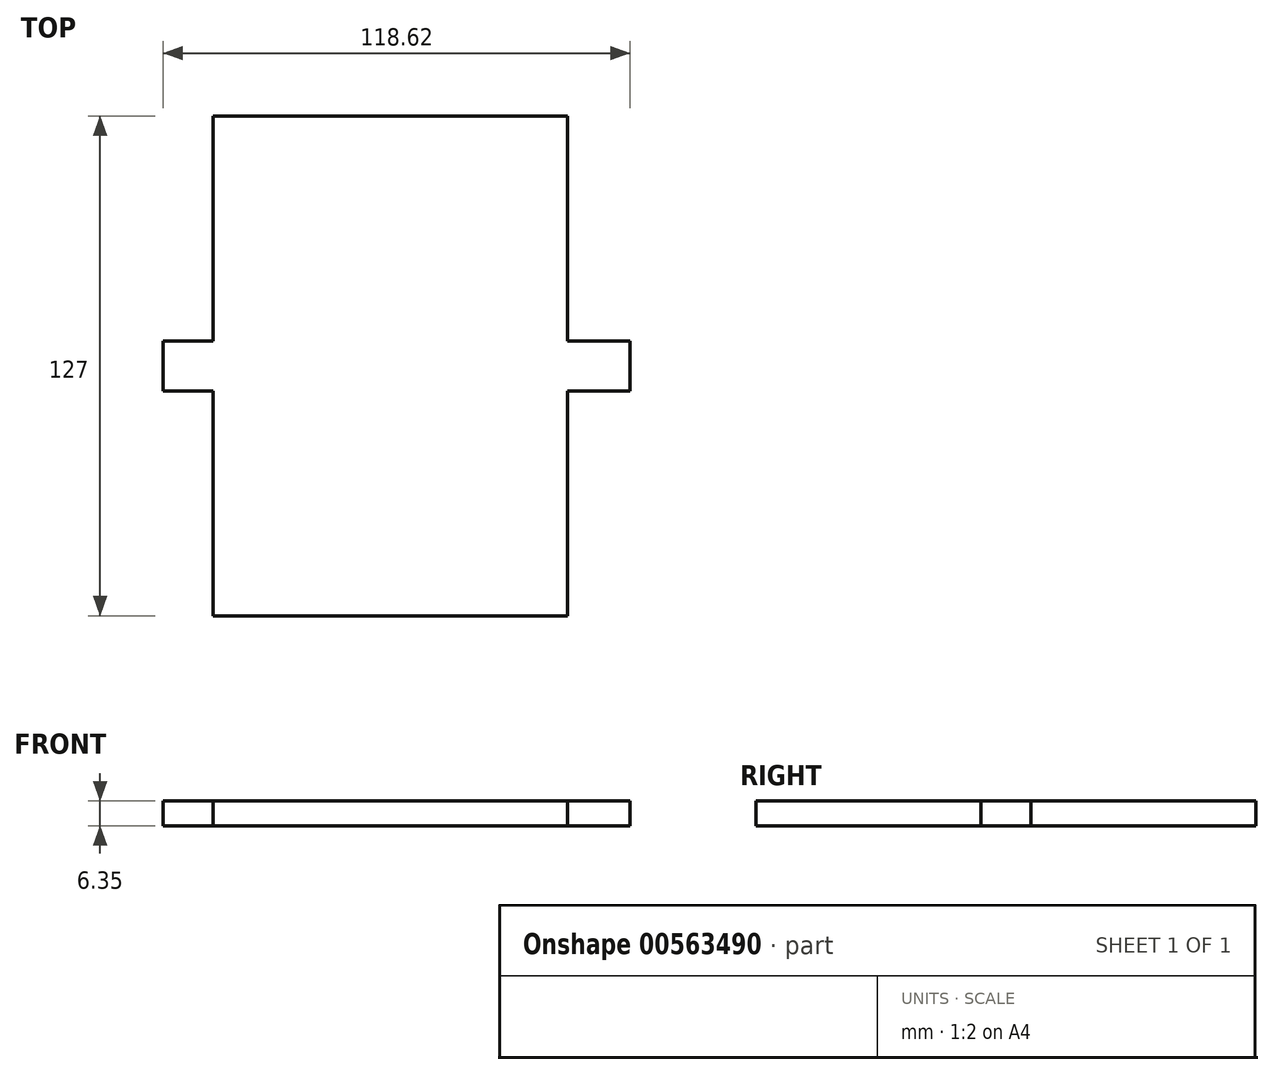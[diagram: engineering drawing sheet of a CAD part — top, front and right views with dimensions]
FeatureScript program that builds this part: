
annotation { "Feature Type Name" : "Feature", "Feature Type Description" : "" }
export const myFeature = defineFeature(function(context is Context, id is Id, definition is map)
    precondition{}
    {
        {
            var Q0;
            Q0=qCreatedBy(makeId("Top.planeOp"),FACE);
            var sketch = newSketch(context, id + "F0", { "sketchPlane" : qUnion([Q0])});
            skLineSegment(sketch, "E0.bottom", {"start": v(0, 0) * mm, "end": v(90.04, 0) * mm});
            skLineSegment(sketch, "E0.top", {"start": v(0, 127) * mm, "end": v(90.04, 127) * mm});
            skLineSegment(sketch, "E0.left", {"start": v(0, 0) * mm, "end": v(0, 57.15) * mm});
            skLineSegment(sketch, "E1", {"start": v(0, 69.85) * mm, "end": v(-12.7, 69.85) * mm});
            skLineSegment(sketch, "E2", {"start": v(-12.7, 69.85) * mm, "end": v(-12.7, 57.15) * mm});
            skLineSegment(sketch, "E3", {"start": v(-12.7, 57.15) * mm, "end": v(0, 57.15) * mm});
            skLineSegment(sketch, "E4.trimOffspring", {"start": v(0, 69.85) * mm, "end": v(0, 127) * mm});
            skLineSegment(sketch, "E5", {"start": v(90.04, 127) * mm, "end": v(90.04, 69.85) * mm});
            skPoint(sketch, "E0.right.end.orphan", {"position": v(180.09, 127) * mm});
            skPoint(sketch, "E6.orphan", {"position": v(180.09, 0) * mm});
            skLineSegment(sketch, "E7", {"start": v(-12.7, 63.5) * mm, "end": v(90.04, 63.5) * mm});
            skLineSegment(sketch, "E8.bottom", {"start": v(90.04, 69.85) * mm, "end": v(105.92, 69.85) * mm});
            skLineSegment(sketch, "E8.top", {"start": v(90.04, 57.15) * mm, "end": v(105.92, 57.15) * mm});
            skLineSegment(sketch, "E8.right", {"start": v(105.92, 69.85) * mm, "end": v(105.92, 57.15) * mm});
            skLineSegment(sketch, "E9", {"start": v(90.04, 63.5) * mm, "end": v(105.92, 63.5) * mm});
            skLineSegment(sketch, "E10.trimOffspring", {"start": v(90.04, 57.15) * mm, "end": v(90.04, 0) * mm});
            skSolve(sketch);
        }
        {
            var Q0;
            Q0 = qSketchRegion(id + "F0", true);
            extrude(context, id + "F1", {"entities" : qUnion([Q0]), "depth" : 6.35 * mm, "offsetDistance" : 25.4 * mm});
        }
    });
